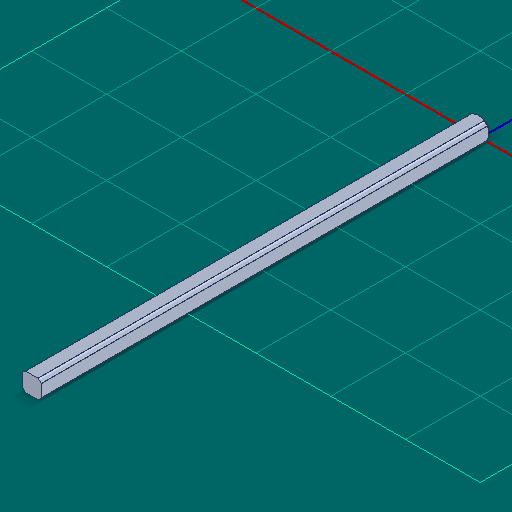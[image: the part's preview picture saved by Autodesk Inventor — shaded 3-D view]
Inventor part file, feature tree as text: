
AUTODESK INVENTOR PART (.ipt)
format: ipt  version: 2025 (Build 290162000, 162)  size: 178,688 bytes
history: native  units: in
note: dims shown in document units (in); Inventor stores cm internally (conversion verified against a paired STEP export)
features: other x50, extrude x2, sketch x2, thicken_offset x1
ambient origin geometry x8: Origin, YZ Plane, XZ Plane, XY Plane, X Axis, Y Axis, Z Axis, Center Point
bodies: Solid1 (feature_tree)
feature tree (55):
  other  "Table"
  other  "Shaft HS 0.5 in"
  other  "Shaft HS 1.0 in"
  other  "Shaft HS 1.5 in"
  other  "Shaft HS 2.0 in"
  other  "Shaft HS 2.5 in"
  other  "Shaft HS 3.0 in"
  other  "Shaft HS 3.5 in"
  other  "Shaft HS 4.0 in"
  other  "Shaft HS 4.5 in"
  other  "Shaft HS 5.0 in"
  other  "Shaft HS 5.5 in"
  other  "Shaft HS 6.0 in"
  other  "Shaft HS 6.5 in"
  other  "Shaft HS 7.0 in"
  other  "Shaft HS 7.5 in"
  other  "Shaft HS 8.0 in"
  other  "Shaft HS 8.5 in"
  other  "Shaft HS 9.0 in"
  other  "Shaft HS 9.5 in"
  other  "Shaft HS 10.0 in"
  other  "Shaft HS 10.5 in"
  other  "Shaft HS 11.0 in"
  other  "Shaft HS 11.5 in"
  other  "Shaft HS 12.0 in"
  other  "Shaft HS 12.5 in"
  other  "Shaft HS 13.0 in"
  other  "Shaft HS 13.5 in"
  other  "Shaft HS 14.0 in"
  other  "Shaft HS 14.5 in"
  other  "Shaft HS 15.0 in"
  other  "Shaft HS 15.5 in"
  other  "Shaft HS 16.0 in"
  other  "Shaft HS 16.5 in"
  other  "Shaft HS 17.0 in"
  other  "Shaft HS 17.5 in"
  other  "Shaft HS 18.0 in"
  other  "Shaft HS 18.5 in"
  other  "Shaft HS 19.0 in"
  other  "Shaft HS 19.5 in"
  other  "Shaft HS 20.0 in"
  other  "Shaft HS 20.5 in"
  other  "Shaft HS 21.0 in"
  other  "Shaft HS 21.5 in"
  other  "Shaft HS 22.0 in"
  other  "Shaft HS 22.5 in"
  other  "Shaft HS 23.0 in"
  other  "Shaft HS 23.5 in"
  other  "Shaft HS 24.0 in"
  extrude  "Extrusion1"  Depth=12.1875in
  thicken_offset  "Thicken1"
  extrude  "Extrusion2"  Depth=18.125in
  sketch  "Sketch2"  dims[d0=0.0625in d1=0.0in d2=12.1875in]
  sketch  "Sketch3"  dims[d3=12.125in d4=18.125in d5=0.0in]
  other  "Cut-Revolve3"
